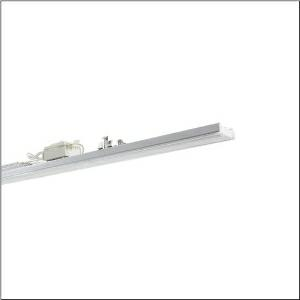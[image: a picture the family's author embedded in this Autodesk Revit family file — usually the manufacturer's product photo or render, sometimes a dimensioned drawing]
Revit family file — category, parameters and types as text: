
# Revit family: licross_21_recessed_mo_52tl12dv4dxgd
name_source: partatom
category: Lighting Fixtures
units: mm (PartAtom-declared; Revit-internal decimal feet)

## family parameters
Cut with Voids When Loaded = No
Host = Face
Light Source = No
Part Type = Normal
Room Calculation Point = No
Round Connector Dimension = Use Diameter
Shared = No

## types (1)
- --- (1 x LED, 13000 lm, 71 W, 4000K)
    Apparent Load = 71 VA
    CIE Flux Codes = 72 92 99 100 100
    Color Rendering = 80
    Color Temperature = 4000K
    Default Elevation = 1800 mm
    Description = Licross 21 Recessed MO, luminaire insert, of sheet steel, galvanised, coil coated, white, length: 2.250mm, width: 66mm, height: 67mm, LED rated luminous flux: 13.000lm, light colour: 840, SDCM (Standard Deviation of Colour Matching)MacAdam ≤ 3 SDCM (initial), control gear: DALI 2 (for two DALI lines), with plug, 6-pole, with phase selection, mains connection: 220..240V, AC/DC, 0/50..60Hz, rated input power: 71W, internal wiring halogen-free, for central battery installations according to EN 60598-2-22, for emergency light function, without changeover relay, primary optical cover: cover, of PMMA, light emission: direct distribution, primary light characteristic: symmetric, protection rating (complete): IP40, insulation class (complete): insulation class I (protective earthing), certification: CE, ENEC, VDE, UKCA, protection symbol: D if used in an environment without relevant dust loads with corresponding accessories, impact resistance: IK06, permissible ambient temperature for indoor applications: -25..+35°C, standard: EN 60598-2-22, corresponds to IFS (International Featured Standards) requirements for safety and quality in the food industry, reducing of maximum allowable ambient temperature of 5°C with ceiling mounting, LABS conformity tested according to VDMA 24364:2018-05, The light source and the operating device comply with the requirements of the Ecodesign Regulation (EU) 2019/2020 and are replaceable in accordance with this regulation, packaging unit: 1 piece
    Height = 58 mm
    Lamp = 1 x LED
    Lamp Light Flux = 13000 lm
    Lamp Power = 71 W
    Lamp count = 1
    Length = 2250 mm
    Luminous efficacy = 183 lm/W
    Manufacturer = Siteco
    ModVariant = No
    Model = 52TL12DV4DXGD
    Mounting Place = Ceiling
    Mounting Type = Pendant
    Number of Poles = 1
    OnlyDefault = Yes
    Power Factor = 1
    Product Name = Licross 21 Recessed MO
    Product group = luminaire insert | ceiling pendant
    ProductGroupID = 901
    Protection Class = Protection class I
    Protection Degree = IP 40
    RLX_Detail_Level = 1
    RLX_Emergency_Light_Flux = 0 lm
    RLX_Emergency_Type = 0
    RLX_Emergency_Type_DB = No
    RlxData = <blob elided: 30405 chars, md5=cf964fd3>
    Socket = socket
    Standby Power = 0 W
    System Light Flux = 13000 lm
    System Power = 71 W
    Type Comments = : AC-mode, luminous flux: 100 % | dim-lin: 254 | 324 mA
    Type Image = l_1296930.jpg
    URL = http://relux.com
    VarID = @adj_113139
    Voltage = 0 V
    Weight = 0.00 kg
    Width = 66 mm

## geometry (parser evidence)
native form markers: Blend x4, Sweep x11
no freeform markers — native parametric forms only
